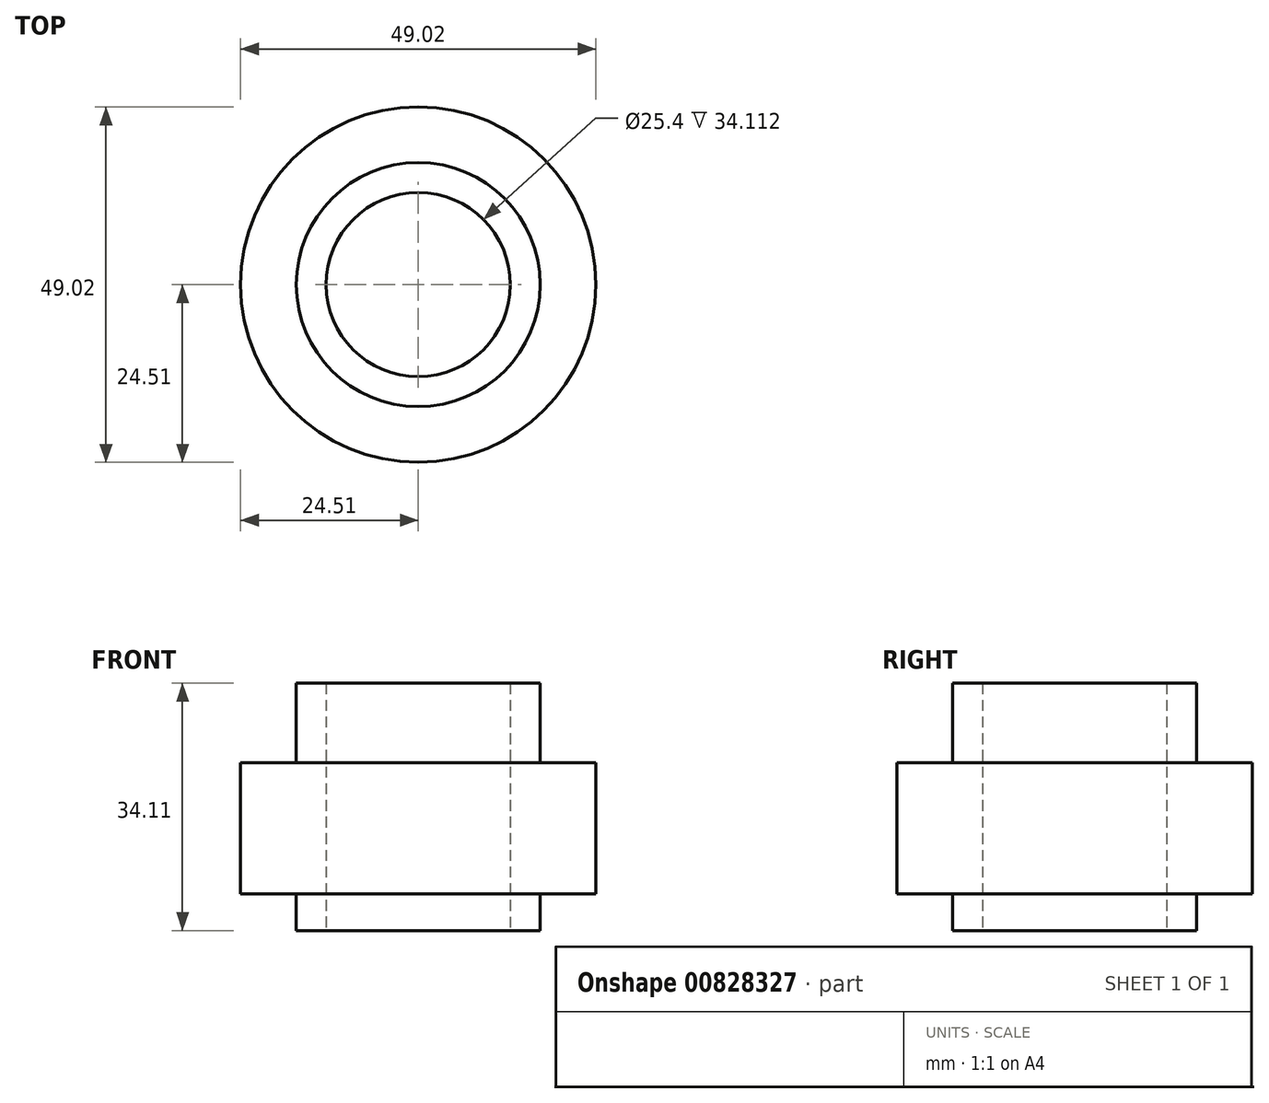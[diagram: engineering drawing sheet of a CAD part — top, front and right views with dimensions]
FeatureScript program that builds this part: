
annotation { "Feature Type Name" : "Feature", "Feature Type Description" : "" }
export const myFeature = defineFeature(function(context is Context, id is Id, definition is map)
    precondition{}
    {
        {
            var Q0;
            Q0=qCreatedBy(makeId("Top.planeOp"),FACE);
            var sketch = newSketch(context, id + "F0", { "sketchPlane" : qUnion([Q0])});
            skCircle(sketch, "E0", {"center": v(0, 0) * mm, "radius": 24.51 * mm});
            skCircle(sketch, "E1", {"center": v(0, 0) * mm, "radius": 16.83 * mm});
            skCircle(sketch, "E2", {"center": v(0, 0) * mm, "radius": 12.7 * mm});
            skSolve(sketch);
        }
        {
            var Q0;
            Q0=makeQuery(id+"F0.imprint","IMPRINT",FACE,{"disambiguationData":[TD([[makeQuery(id+"F0.imprint","IMPRINT",EDGE,{"derivedFrom":sQuery(id+"F0.wireOp",EDGE,"E2")}),1.0]])]});
            var Q1;
            Q1=makeQuery(id+"F0.imprint","IMPRINT",FACE,{"disambiguationData":[TD([[makeQuery(id+"F0.imprint","IMPRINT",EDGE,{"derivedFrom":sQuery(id+"F0.wireOp",EDGE,"E1")}),1.0]])]});
            var Q2;
            Q2=makeQuery(id+"F0.imprint","IMPRINT",FACE,{"disambiguationData":[TD([[makeQuery(id+"F0.imprint","IMPRINT",EDGE,{"derivedFrom":sQuery(id+"F0.wireOp",EDGE,"E0")}),1.0]])]});
            var Q3;
            Q3=sQuery(id+"F0.wireOp",EDGE,"E0");
            var Q4;
            Q4=sQuery(id+"F0.wireOp",EDGE,"E2");
            extrude(context, id + "F1", {"entities" : qUnion([Q0, Q1, Q2]), "surfaceEntities" : qUnion([Q3, Q4]), "depth" : 18.1 * mm, "offsetDistance" : 25.4 * mm});
        }
        {
            var Q0;
            Q0=makeQuery(id+"F0.imprint","IMPRINT",FACE,{"disambiguationData":[TD([[makeQuery(id+"F0.imprint","IMPRINT",EDGE,{"derivedFrom":sQuery(id+"F0.wireOp",EDGE,"E1")}),1.0]])]});
            extrude(context, id + "F2", {"entities" : qUnion([Q0]), "operationType" : NewBodyOperationType.ADD, "depth" : 29.03 * mm, "offsetDistance" : 25.4 * mm, "hasSecondDirection" : true, "secondDirectionOppositeDirection" : true, "secondDirectionDepth" : 5.08 * mm});
        }
        {
            var Q0;
            Q0=makeQuery(id+"F2.boolean.opBoolean","SPLIT",FACE,{"disambiguationData":[TD([makeQuery(id+"F2.opExtrude","SWEPT_FACE",FACE,{"disambiguationData":[OSD([sQuery(id+"F0.wireOp",EDGE,"E2")])]})])],"derivedFrom":makeQuery(id+"F1.opExtrude","CAP_FACE",FACE,{"disambiguationData":[OSD([sQuery(id+"F0.wireOp",EDGE,"E0")])],"isStart":true})});
            extrude(context, id + "F3", {"entities" : qUnion([Q0]), "operationType" : NewBodyOperationType.REMOVE, "endBound" : BoundingType.THROUGH_ALL, "oppositeDirection" : true, "depth" : 25.4 * mm, "offsetDistance" : 25.4 * mm});
        }
    });
